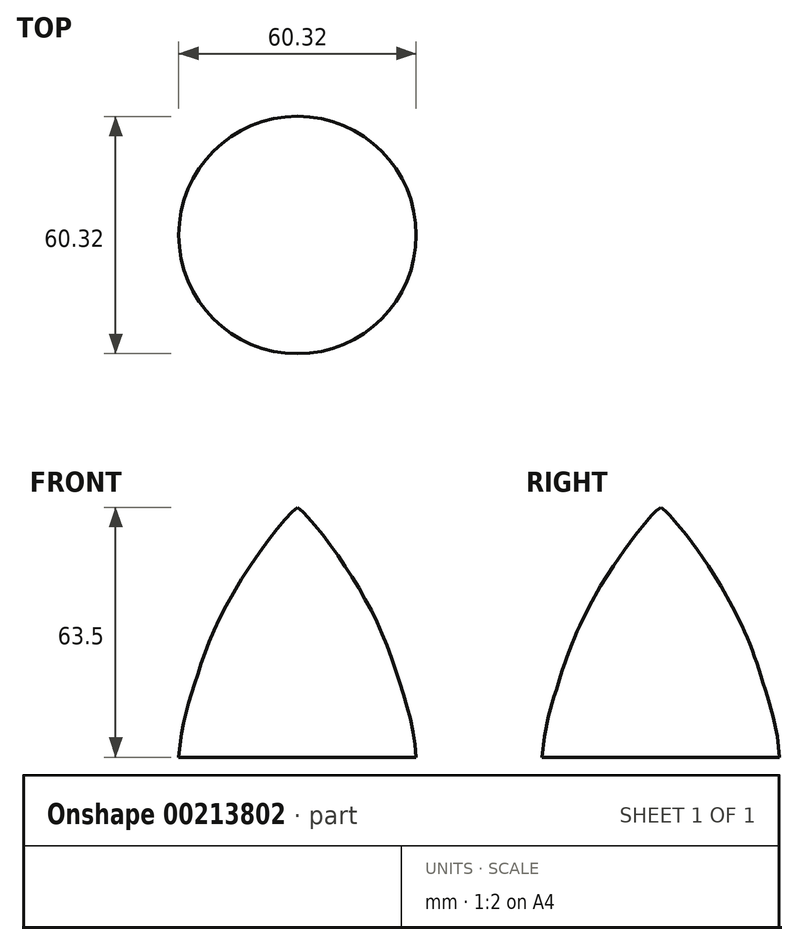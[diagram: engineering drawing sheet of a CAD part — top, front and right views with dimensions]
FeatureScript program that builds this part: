
annotation { "Feature Type Name" : "Feature", "Feature Type Description" : "" }
export const myFeature = defineFeature(function(context is Context, id is Id, definition is map)
    precondition{}
    {
        {
            var Q0;
            Q0=qCreatedBy(makeId("Front.planeOp"),FACE);
            var sketch = newSketch(context, id + "F0", { "sketchPlane" : qUnion([Q0])});
            skFitSpline(sketch, "E0", {"points": [v(-30.16, 0) * mm, v(-26.24, 18.18) * mm, v(-17.33, 39.94) * mm, v(0, 63.5) * mm], "startDerivative": vector(5.06, 74.42) * mm, "endDerivative": vector(28.49, 19.5) * mm});
            skLineSegment(sketch, "E1", {"start": v(-30.16, 0) * mm, "end": v(0, 0) * mm});
            skLineSegment(sketch, "E2", {"start": v(0, 0) * mm, "end": v(0, 63.5) * mm});
            skSolve(sketch);
        }
        {
            var Q0;
            Q0=makeQuery(id+"F0.imprint","IMPRINT",FACE,{"disambiguationData":[TD([[makeQuery(id+"F0.imprint","IMPRINT",EDGE,{"derivedFrom":sQuery(id+"F0.wireOp",EDGE,"E0")}),-1.0]])]});
            var Q1;
            Q1=sQuery(id+"F0.wireOp",EDGE,"E2");
            revolve(context, id + "F1", {"entities" : qUnion([Q0]), "axis" : qUnion([Q1]), "revolveType" : RevolveType.FULL});
        }
    });
